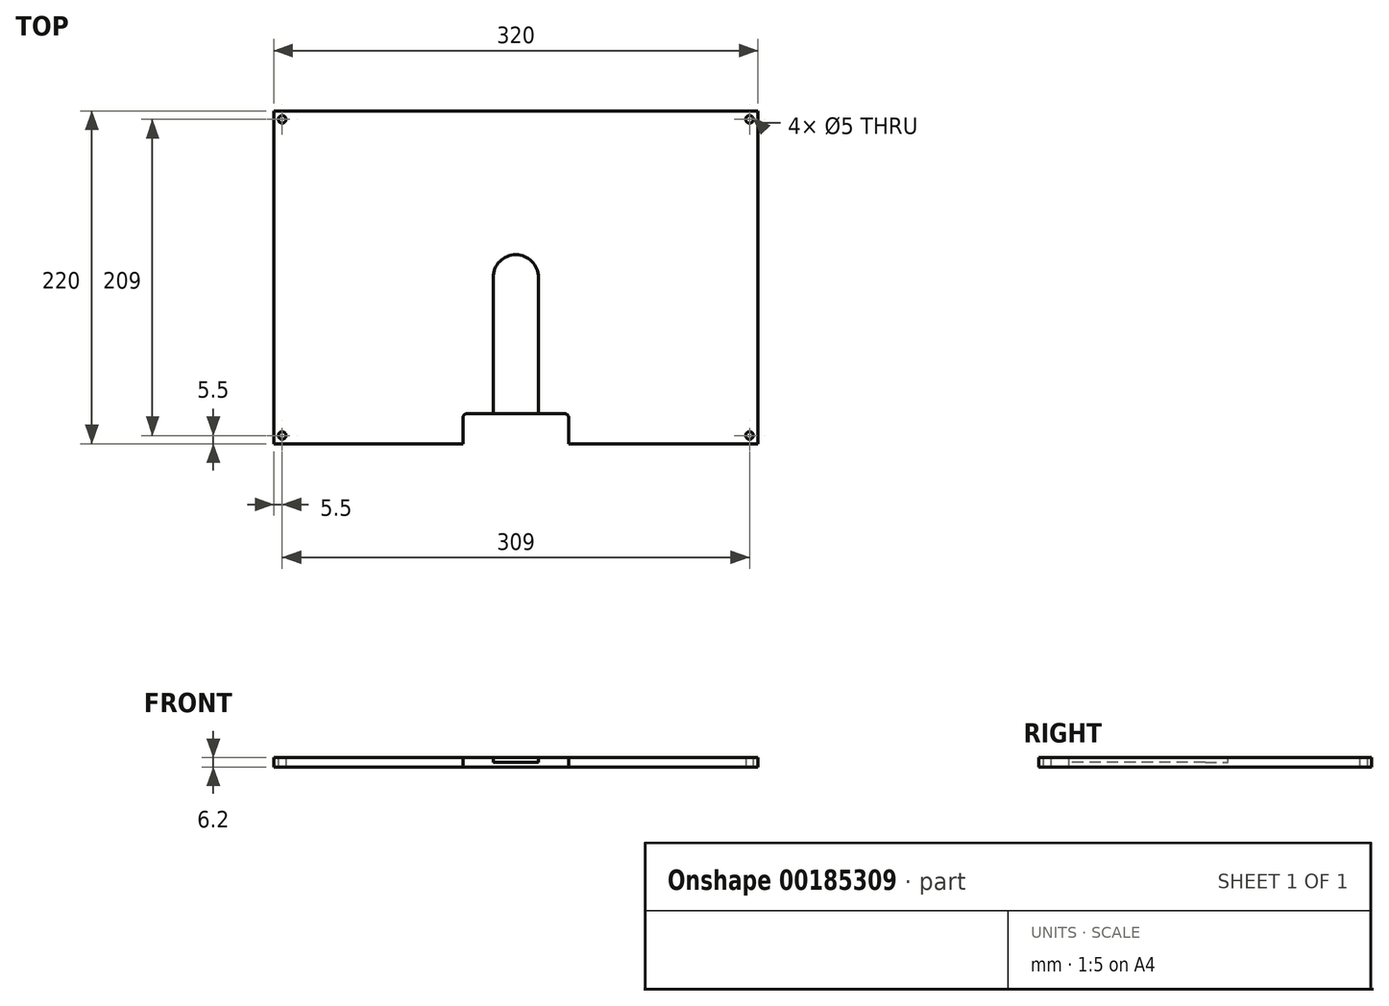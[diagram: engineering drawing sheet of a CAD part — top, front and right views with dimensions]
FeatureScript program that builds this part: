
annotation { "Feature Type Name" : "Feature", "Feature Type Description" : "" }
export const myFeature = defineFeature(function(context is Context, id is Id, definition is map)
    precondition{}
    {
        {
            var Q0;
            Q0=qCreatedBy(makeId("Top.planeOp"),FACE);
            var sketch = newSketch(context, id + "F0", { "sketchPlane" : qUnion([Q0])});
            skLineSegment(sketch, "E0.bottom", {"start": v(160, -110) * mm, "end": v(-160, -110) * mm});
            skLineSegment(sketch, "E0.top", {"start": v(160, 110) * mm, "end": v(-160, 110) * mm});
            skLineSegment(sketch, "E0.left", {"start": v(160, -110) * mm, "end": v(160, 110) * mm});
            skLineSegment(sketch, "E0.right", {"start": v(-160, -110) * mm, "end": v(-160, 110) * mm});
            skPoint(sketch, "E0.middle", {"position": v(0, 0) * mm});
            skCircle(sketch, "E1", {"center": v(-154.5, -104.5) * mm, "radius": 2.5 * mm});
            skCircle(sketch, "E2", {"center": v(154.5, -104.5) * mm, "radius": 2.5 * mm});
            skCircle(sketch, "E3", {"center": v(-154.5, 104.5) * mm, "radius": 2.5 * mm});
            skCircle(sketch, "E4", {"center": v(154.5, 104.5) * mm, "radius": 2.5 * mm});
            skSolve(sketch);
        }
        {
            var Q0;
            Q0 = qSketchRegion(id + "F0", true);
            extrude(context, id + "F1", {"entities" : qUnion([Q0]), "depth" : 6.2 * mm});
        }
        {
            var Q0;
            Q0=makeQuery(id+"F1.opExtrude","CAP_FACE",FACE,{"disambiguationData":[OSD([sQuery(id+"F0.wireOp",EDGE,"E0.bottom"),sQuery(id+"F0.wireOp",EDGE,"E0.top"),sQuery(id+"F0.wireOp",EDGE,"E0.left"),sQuery(id+"F0.wireOp",EDGE,"E0.right"),sQuery(id+"F0.wireOp",EDGE,"E1"),sQuery(id+"F0.wireOp",EDGE,"E2"),sQuery(id+"F0.wireOp",EDGE,"E3"),sQuery(id+"F0.wireOp",EDGE,"E4")])],"isStart":false});
            var sketch = newSketch(context, id + "F2", { "sketchPlane" : qUnion([Q0])});
            skCircle(sketch, "E5", {"center": v(0, 0) * mm, "radius": 15 * mm});
            skLineSegment(sketch, "E6.bottom", {"start": v(-15, 0) * mm, "end": v(15, 0) * mm});
            skLineSegment(sketch, "E6.top", {"start": v(-15, -110) * mm, "end": v(15, -110) * mm});
            skLineSegment(sketch, "E6.left", {"start": v(-15, 0) * mm, "end": v(-15, -110) * mm});
            skLineSegment(sketch, "E6.right", {"start": v(15, 0) * mm, "end": v(15, -110) * mm});
            skSolve(sketch);
        }
        {
            var Q0;
            {var subQ0=sQuery(id+"F2.wireOp",EDGE,"E6.bottom");Q0=makeQuery(id+"F2.imprint","IMPRINT",FACE,{"disambiguationData":[TD([[makeQuery(id+"F2.imprint","IMPRINT",EDGE,{"derivedFrom":subQ0}),1.0]])]});}
            var Q1;
            Q1=makeQuery(id+"F2.imprint","IMPRINT",FACE,{"disambiguationData":[TD([[makeQuery(id+"F2.imprint","IMPRINT",EDGE,{"derivedFrom":sQuery(id+"F2.wireOp",EDGE,"E6.top")}),-1.0]])]});
            var Q2;
            {var subQ0=sQuery(id+"F2.wireOp",EDGE,"E6.bottom");Q2=makeQuery(id+"F2.imprint","IMPRINT",FACE,{"disambiguationData":[TD([[makeQuery(id+"F2.imprint","IMPRINT",EDGE,{"derivedFrom":subQ0}),-1.0]])]});}
            extrude(context, id + "F3", {"entities" : qUnion([Q0, Q1, Q2]), "operationType" : NewBodyOperationType.REMOVE, "oppositeDirection" : true, "depth" : 3 * mm});
        }
        {
            var Q0;
            Q0=makeQuery(id+"F1.opExtrude","CAP_FACE",FACE,{"disambiguationData":[OSD([sQuery(id+"F0.wireOp",EDGE,"E0.bottom"),sQuery(id+"F0.wireOp",EDGE,"E0.top"),sQuery(id+"F0.wireOp",EDGE,"E0.left"),sQuery(id+"F0.wireOp",EDGE,"E0.right"),sQuery(id+"F0.wireOp",EDGE,"E1"),sQuery(id+"F0.wireOp",EDGE,"E2"),sQuery(id+"F0.wireOp",EDGE,"E3"),sQuery(id+"F0.wireOp",EDGE,"E4")])],"isStart":false});
            var sketch = newSketch(context, id + "F4", { "sketchPlane" : qUnion([Q0])});
            skLineSegment(sketch, "E7.bottom", {"start": v(-35, -110) * mm, "end": v(35, -110) * mm});
            skLineSegment(sketch, "E7.top", {"start": v(-35, -90) * mm, "end": v(35, -90) * mm});
            skLineSegment(sketch, "E7.left", {"start": v(-35, -110) * mm, "end": v(-35, -90) * mm});
            skLineSegment(sketch, "E7.right", {"start": v(35, -110) * mm, "end": v(35, -90) * mm});
            skSolve(sketch);
        }
        {
            var Q0;
            Q0 = qSketchRegion(id + "F4", true);
            extrude(context, id + "F5", {"entities" : qUnion([Q0]), "operationType" : NewBodyOperationType.REMOVE, "oppositeDirection" : true, "depth" : 25 * mm});
        }
        {
            var Q0;
            Q0=makeQuery(id+"F5.boolean.opBoolean","COPY",EDGE,{"derivedFrom":makeQuery(id+"F5.opExtrude","SWEPT_EDGE",EDGE,{"disambiguationData":[OSD([sQuery(id+"F4.wireOp",EDGE,"E7.top"),sQuery(id+"F4.wireOp",EDGE,"E7.right")])]})});
            var Q1;
            Q1=makeQuery(id+"F5.boolean.opBoolean","COPY",EDGE,{"derivedFrom":makeQuery(id+"F5.opExtrude","SWEPT_EDGE",EDGE,{"disambiguationData":[OSD([sQuery(id+"F4.wireOp",EDGE,"E7.top"),sQuery(id+"F4.wireOp",EDGE,"E7.left")])]})});
            fillet(context, id + "F6", {"entities" : qUnion([Q0, Q1]), "radius" : 3 * mm, "tangentPropagation" : true, "allowEdgeOverflow" : false});
        }
    });
